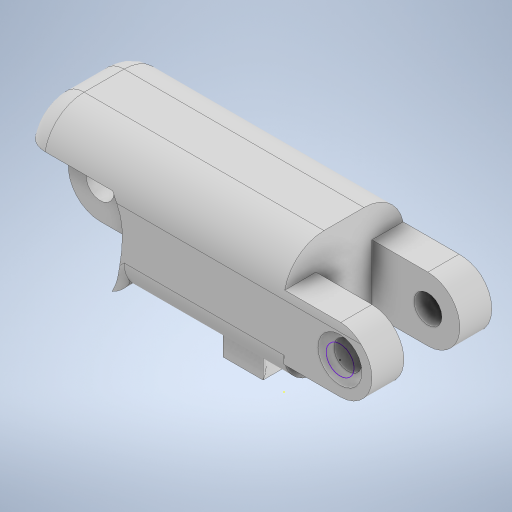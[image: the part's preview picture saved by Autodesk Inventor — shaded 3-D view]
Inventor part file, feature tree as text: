
AUTODESK INVENTOR PART (.ipt)
format: ipt  version: 2024 (Build 280153000, 153)  size: 551,424 bytes
history: native  units: mm
features: sketch x17, extrude x14, fillet x7, other x1
ambient origin geometry x8: Origin, YZ Plane, XZ Plane, XY Plane, X Axis, Y Axis, Z Axis, Center Point
bodies: Body1 (feature_tree)
feature tree (39):
  other  "Твердое тело1"
  extrude  "Выдавливание1"  Depth=15.0mm
  fillet  "Сопряжение1"  Radius=20.0mm
  extrude  "Выдавливание4"  Depth=15.0mm TaperAngle=0.0deg
  extrude  "Выдавливание5"  Depth=4.0mm
  extrude  "Выдавливание6"  Depth=8.0mm
  extrude  "Выдавливание7"  Depth=8.0mm
  extrude  "Выдавливание8"  Depth=4.0mm
  extrude  "Выдавливание9"  Depth=7.0mm
  extrude  "Выдавливание10"  Depth=3.5mm
  fillet  "Сопряжение4"  [1 undecoded]
  extrude  "Выдавливание11"  Depth=4.0mm
  extrude  "Выдавливание12"  Depth=4.0mm
  fillet  "Сопряжение6"  [1 undecoded]
  sketch  "Эскиз14"
  fillet  "Сопряжение7"  Radius=8.0mm
  fillet  "Сопряжение8"  Radius=8.0mm
  extrude  "Выдавливание13"  Depth=11.0mm
  extrude  "Выдавливание14"  Depth=4.0mm
  extrude  "Выдавливание15"  Depth=3.5mm
  sketch  "Эскиз18"
  sketch  "Эскиз19"
  extrude  "Выдавливание16"  TaperAngle=0.0deg  [1 undecoded]
  fillet  "Сопряжение9"  Radius=4.0mm
  fillet  "Сопряжение10"  Radius=4.0mm
  sketch  "Эскиз1"
  sketch  "Эскиз4"
  sketch  "Эскиз5"
  sketch  "Эскиз7"
  sketch  "Эскиз8"
  sketch  "Эскиз9"
  sketch  "Эскиз10"
  sketch  "Эскиз11"
  sketch  "Эскиз12"
  sketch  "Эскиз13"
  sketch  "Эскиз15"
  sketch  "Эскиз16"
  sketch  "Эскиз17"
  sketch  "Эскиз20"
note: 3 required parameter values undecoded (feature->parameter linkage not recoverable at this tier; creation-order binding heuristic only, values carry confidence <= 0.55)
